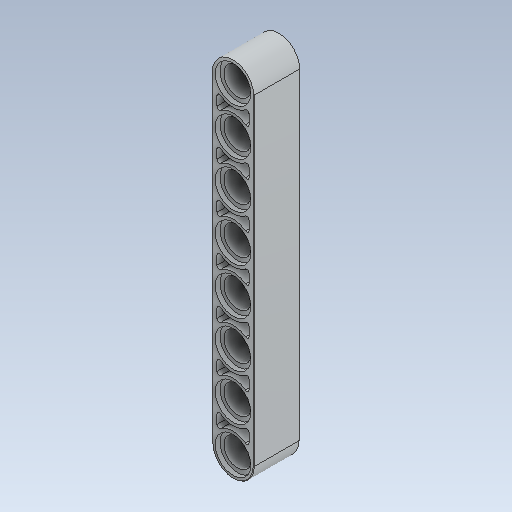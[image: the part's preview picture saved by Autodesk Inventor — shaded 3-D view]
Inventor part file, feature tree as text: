
AUTODESK INVENTOR PART (.ipt)
format: ipt  version: 2020 (Build 240168000, 168)  size: 401,408 bytes
history: native  units: mm
features: other x4, extrude x1, sketch x1
ambient origin geometry x8: Origin, YZ Plane, XZ Plane, XY Plane, X Axis, Y Axis, Z Axis, Center Point
bodies: Body1 (feature_tree)
feature tree (6):
  other  "Component2.ipt"
  extrude  "Extrusão1"  Depth=10.0mm TaperAngle=0.0deg
  other  "Sólido1::Component2.ipt"
  other  "OperaçãoIdentificador1"
  sketch  "Esboço1"  dims[d0=10.0mm d1=11.75mm d2=0.0mm]
  other  "Sólido1"
